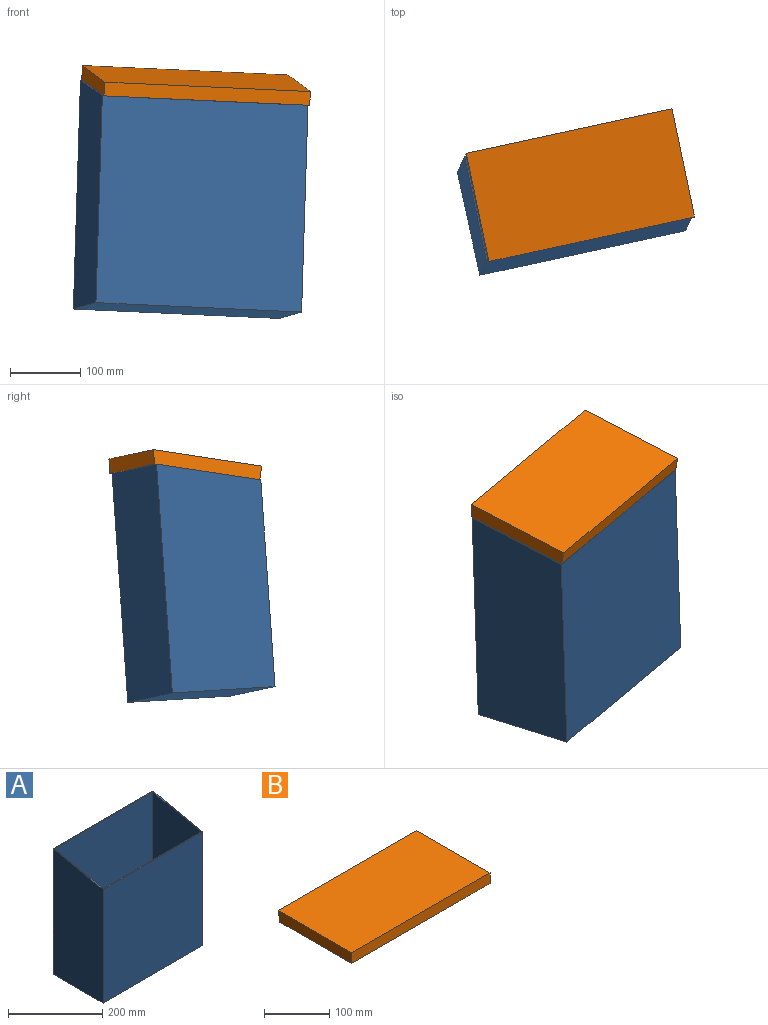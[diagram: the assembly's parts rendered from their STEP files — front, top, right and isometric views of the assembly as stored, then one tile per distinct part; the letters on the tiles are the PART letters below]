
ASSEMBLY  parts=2 mates=1
PART A: 11 faces, bbox 300x150x327 mm
  f0: plane 300x295.44mm, normal (0,-1,0), area 88633.2mm2, adj f1,f3,f4,f5
  f1: plane 327x150mm, normal (-1,0,0), area 46683.3mm2, adj f0,f2,f4,f5
  f2: plane 327x300mm, normal (0,1,0), area 98100mm2, adj f1,f3,f4,f5
  f3: plane 327x150mm, normal (1,0,0), area 46683.3mm2, adj f0,f2,f4,f5
  f4: plane 300x150mm, normal (0,0,-1), area 45000mm2, adj f0,f1,f2,f3
  f5: plane 300x150mm, normal (0,-0.21,0.98), area 2273.7mm2, adj f0,f1,f2,f3,f7,f8,f9,f10
  f6: plane 295x145mm, normal (0,0,1), area 42775mm2, adj f7,f8,f9,f10
  f7: plane 323.97x145mm, normal (-1,0,0), area 44764.7mm2, adj f5,f6,f8,f10
  f8: plane 295x293.47mm, normal (0,1,0), area 86573.6mm2, adj f5,f6,f7,f9
  f9: plane 323.97x145mm, normal (1,0,0), area 44764.7mm2, adj f5,f6,f8,f10
  f10: plane 323.97x295mm, normal (0,-1,0), area 95572.3mm2, adj f5,f6,f7,f9
PART B: 11 faces, bbox 300x159.2x20 mm
  f0: plane 300x155mm, normal (0,0,-1), area 2266.1mm2, adj f2,f3,f4,f5,f7,f8,f9,f10
  f1: plane 300x159.21mm, normal (0,0,1), area 47762.2mm2, adj f2,f3,f4,f5
  f2: plane 300x20mm, normal (0,-1,0), area 6000mm2, adj f0,f1,f4,f5
  f3: plane 300x20mm, normal (0,0.98,-0.21), area 6131.3mm2, adj f0,f1,f4,f5
  f4: plane 159.21x20mm, normal (1,0,0), area 3142.1mm2, adj f0,f1,f2,f3
  f5: plane 159.21x20mm, normal (-1,0,0), area 3142.1mm2, adj f0,f1,f2,f3
  f6: plane 295x153.63mm, normal (0,0,-1), area 45319.9mm2, adj f7,f8,f9,f10
  f7: plane 295x17.5mm, normal (0,1,0), area 5162.5mm2, adj f0,f6,f9,f10
  f8: plane 295x17.5mm, normal (0,-0.98,0.21), area 5275.5mm2, adj f0,f6,f9,f10
  f9: plane 153.63x17.5mm, normal (-1,0,0), area 2656.3mm2, adj f0,f6,f7,f8
  f10: plane 153.63x17.5mm, normal (1,0,0), area 2656.3mm2, adj f0,f6,f7,f8
PLACE A rot(axis=(-0.29,0.17,0.94),13deg) t=(-274.89,-26.03,39.88)mm
PLACE B rot(axis=(0.55,0.23,0.8),15deg) t=(-263.53,-4.37,334.18)mm
MATE revolute B.f9 <-> A.f3  axis (-0.98,-0.21,0.04) through (-3.98,206.1,343.45)mm
